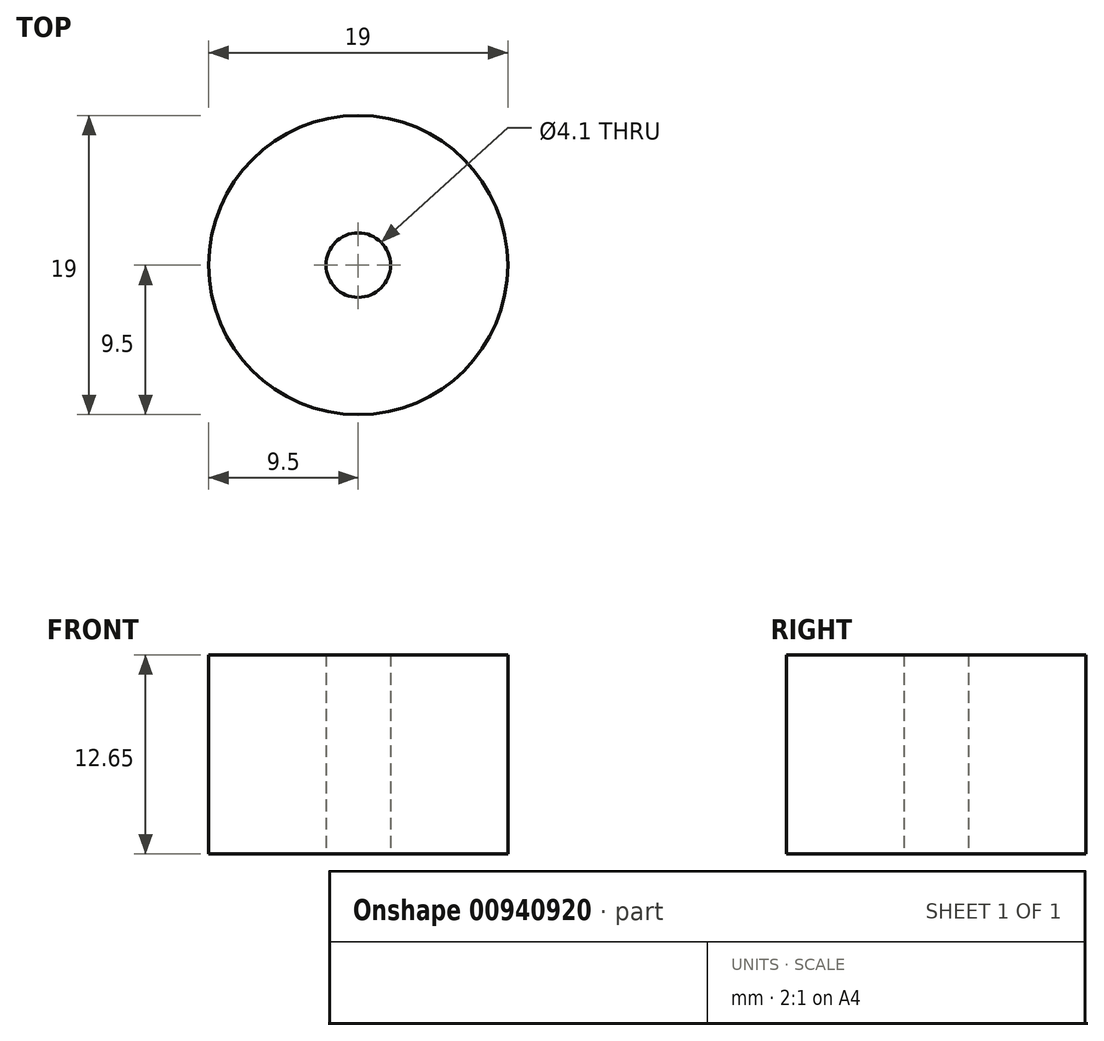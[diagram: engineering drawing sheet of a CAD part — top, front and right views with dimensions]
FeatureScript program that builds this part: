
annotation { "Feature Type Name" : "Feature", "Feature Type Description" : "" }
export const myFeature = defineFeature(function(context is Context, id is Id, definition is map)
    precondition{}
    {
        {
            var Q0;
            Q0=qCreatedBy(makeId("Top.planeOp"),FACE);
            var sketch = newSketch(context, id + "F0", { "sketchPlane" : qUnion([Q0])});
            skCircle(sketch, "E0", {"center": v(0, 0) * mm, "radius": 9.5 * mm});
            skCircle(sketch, "E1", {"center": v(0, 0) * mm, "radius": 2.05 * mm});
            skSolve(sketch);
        }
        {
            var Q0;
            Q0=makeQuery(id+"F0.imprint","IMPRINT",FACE,{"disambiguationData":[TD([[makeQuery(id+"F0.imprint","IMPRINT",EDGE,{"derivedFrom":sQuery(id+"F0.wireOp",EDGE,"E0")}),1.0]])]});
            extrude(context, id + "F1", {"entities" : qUnion([Q0]), "depth" : 12.65 * mm, "offsetDistance" : 25 * mm});
        }
    });
